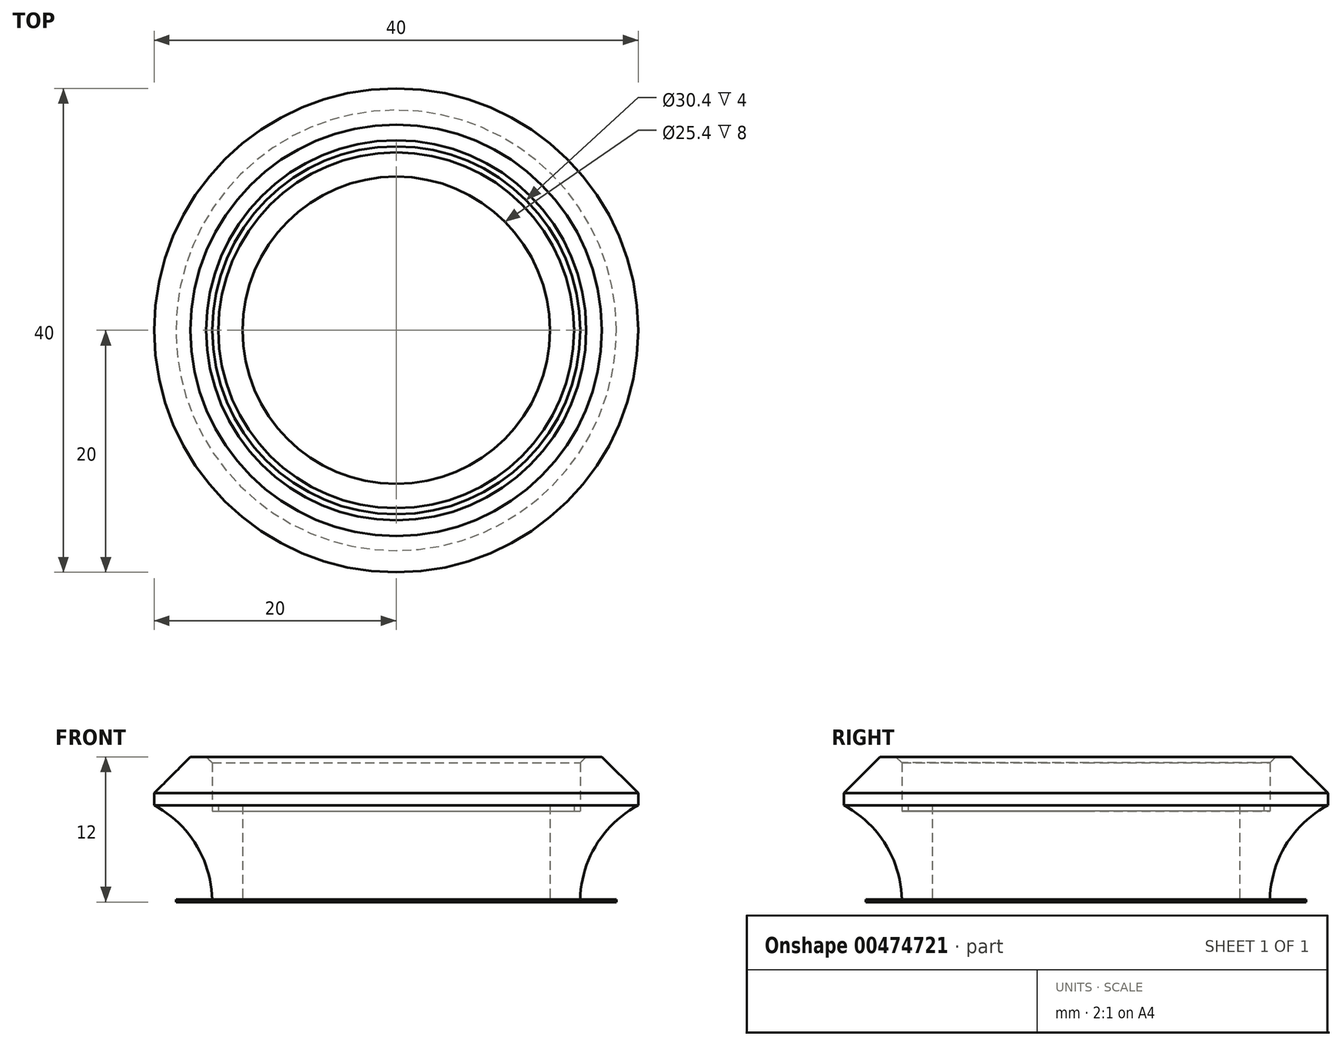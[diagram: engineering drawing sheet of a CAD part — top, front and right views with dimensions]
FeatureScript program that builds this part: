
annotation { "Feature Type Name" : "Feature", "Feature Type Description" : "" }
export const myFeature = defineFeature(function(context is Context, id is Id, definition is map)
    precondition{}
    {
        {
            var Q0;
            Q0=qCreatedBy(makeId("Front.planeOp"),FACE);
            var sketch = newSketch(context, id + "F0", { "sketchPlane" : qUnion([Q0])});
            skLineSegment(sketch, "E0", {"start": v(0, 0) * mm, "end": v(0, 12) * mm, "construction": true});
            skLineSegment(sketch, "E1", {"start": v(12.7, 0) * mm, "end": v(12.7, 8) * mm});
            skLineSegment(sketch, "E2", {"start": v(12.7, 8) * mm, "end": v(14.7, 8) * mm});
            skLineSegment(sketch, "E3", {"start": v(15.2, 7.5) * mm, "end": v(15.2, 12) * mm});
            skLineSegment(sketch, "E4", {"start": v(15.2, 12) * mm, "end": v(17, 12) * mm});
            skLineSegment(sketch, "E5", {"start": v(17, 12) * mm, "end": v(20, 9) * mm});
            skLineSegment(sketch, "E6", {"start": v(20, 9) * mm, "end": v(20, 8) * mm});
            skArc(sketch, "E7", {"start": v(20, 8) * mm, "mid": v(16.5, 4.66) * mm, "end": v(15.2, 0) * mm});
            skLineSegment(sketch, "E8", {"start": v(12.7, 0) * mm, "end": v(15.2, 0) * mm});
            skLineSegment(sketch, "E9", {"start": v(15.2, 0) * mm, "end": v(15.2, 7.5) * mm, "construction": true});
            skLineSegment(sketch, "E10", {"start": v(14.7, 8) * mm, "end": v(14.7, 7.5) * mm});
            skLineSegment(sketch, "E11", {"start": v(14.7, 7.5) * mm, "end": v(15.2, 7.5) * mm});
            skSolve(sketch);
        }
        {
            var Q0;
            Q0=qSketchRegion(id+"F0",true);
            var Q1;
            Q1=sQuery(id+"F0.wireOp",EDGE,"E0");
            revolve(context, id + "F1", {"surfaceOperationType" : NewSurfaceOperationType.NEW, "entities" : qUnion([Q0]), "axis" : qUnion([Q1]), "revolveType" : RevolveType.FULL});
        }
        {
            var Q0;
            Q0=makeQuery(id+"F1.opRevolve","SWEPT_EDGE",EDGE,{"disambiguationData":[OSD([sQuery(id+"F0.wireOp",EDGE,"E3"),sQuery(id+"F0.wireOp",EDGE,"E4")])]});
            chamfer(context, id + "F2", {"entities" : qUnion([Q0]), "width" : 0.5 * mm, "tangentPropagation" : true});
        }
        {
            var Q0;
            Q0=makeQuery(id+"F1.opRevolve","SWEPT_FACE",FACE,{"disambiguationData":[OSD([sQuery(id+"F0.wireOp",EDGE,"E8")])]});
            var sketch = newSketch(context, id + "F3", { "sketchPlane" : qUnion([Q0])});
            skCircle(sketch, "E12", {"center": v(0, 0) * mm, "radius": 18.2 * mm});
            skCircle(sketch, "E13", {"center": v(0, 0) * mm, "radius": 15.2 * mm});
            skSolve(sketch);
        }
        {
            var Q0;
            Q0 = qSketchRegion(id + "F3", true);
            extrude(context, id + "F4", {"entities" : qUnion([Q0]), "operationType" : NewBodyOperationType.ADD, "oppositeDirection" : true, "depth" : 0.2 * mm, "offsetDistance" : 25 * mm});
        }
    });
